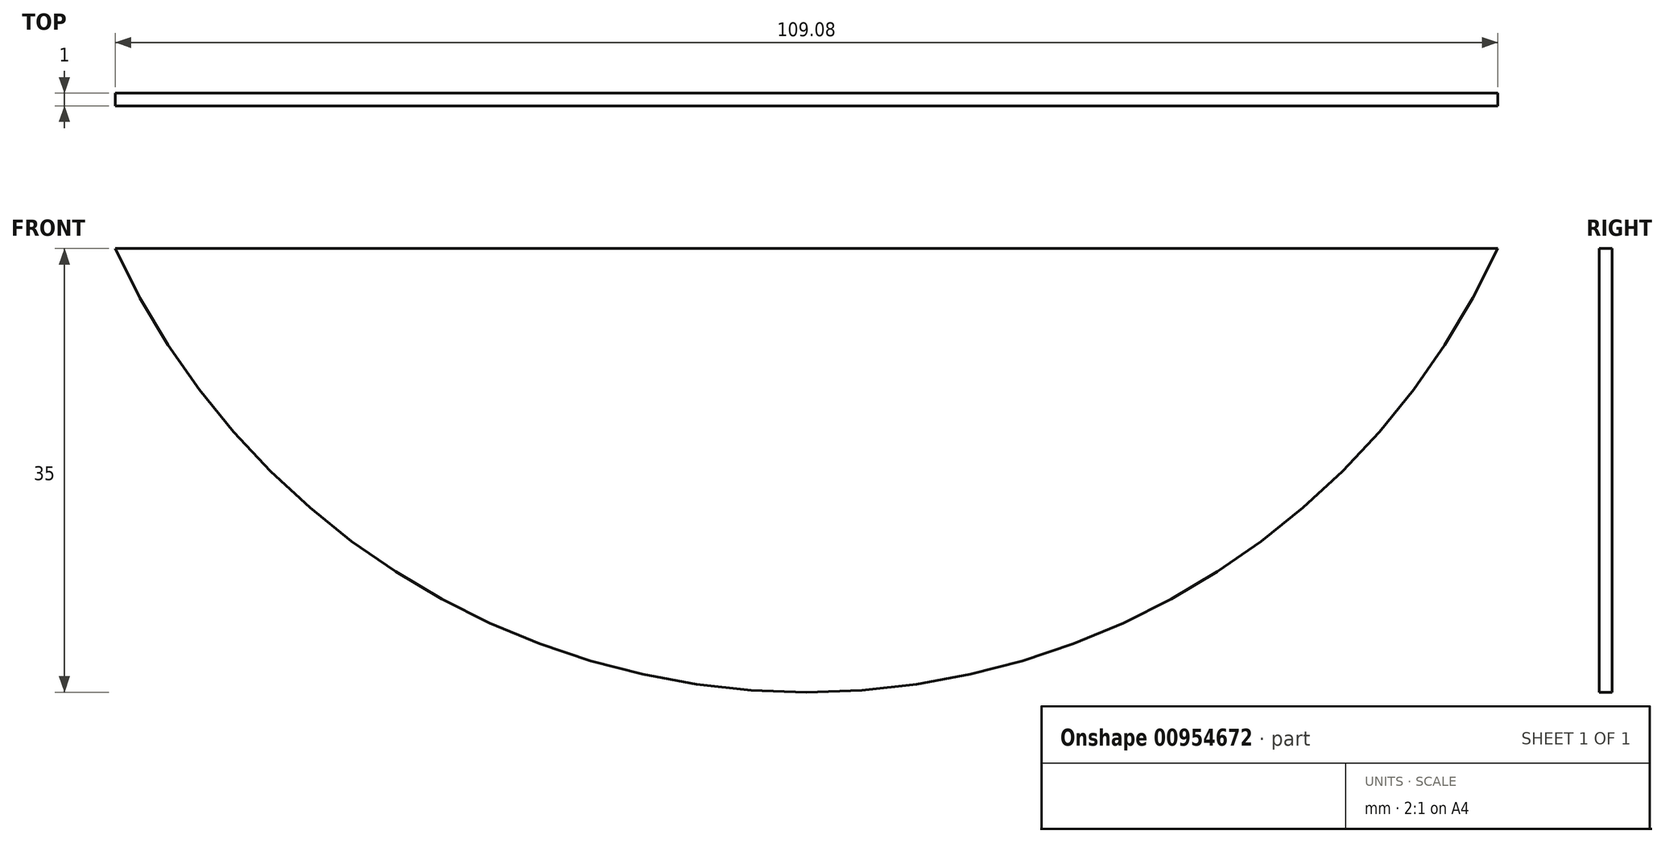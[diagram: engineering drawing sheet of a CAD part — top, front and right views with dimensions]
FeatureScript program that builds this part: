
annotation { "Feature Type Name" : "Feature", "Feature Type Description" : "" }
export const myFeature = defineFeature(function(context is Context, id is Id, definition is map)
    precondition{}
    {
        {
            var Q0;
            Q0=qCreatedBy(makeId("Front.planeOp"),FACE);
            var sketch = newSketch(context, id + "F0", { "sketchPlane" : qUnion([Q0])});
            skArc(sketch, "E0", {"start": v(-54.54, -25) * mm, "mid": v(0, -60) * mm, "end": v(54.54, -25) * mm});
            skLineSegment(sketch, "E1.bottom", {"start": v(54.54, -25) * mm, "end": v(-54.54, -25) * mm});
            skPoint(sketch, "E1.left.start.orphan", {"position": v(63.03, -25) * mm});
            skPoint(sketch, "E2.orphan", {"position": v(63.03, 25) * mm});
            skPoint(sketch, "E1.top.end.orphan", {"position": v(-63.03, 25) * mm});
            skPoint(sketch, "E3.orphan", {"position": v(-63.03, -25) * mm});
            skSolve(sketch);
        }
        {
            var Q0;
            Q0=makeQuery(id+"F0.imprint","IMPRINT",FACE,{"disambiguationData":[TD([[makeQuery(id+"F0.imprint","IMPRINT",EDGE,{"derivedFrom":sQuery(id+"F0.wireOp",EDGE,"E0")}),1.0]])]});
            extrude(context, id + "F1", {"entities" : qUnion([Q0]), "depth" : 1 * mm, "offsetDistance" : 25.4 * mm});
        }
    });
